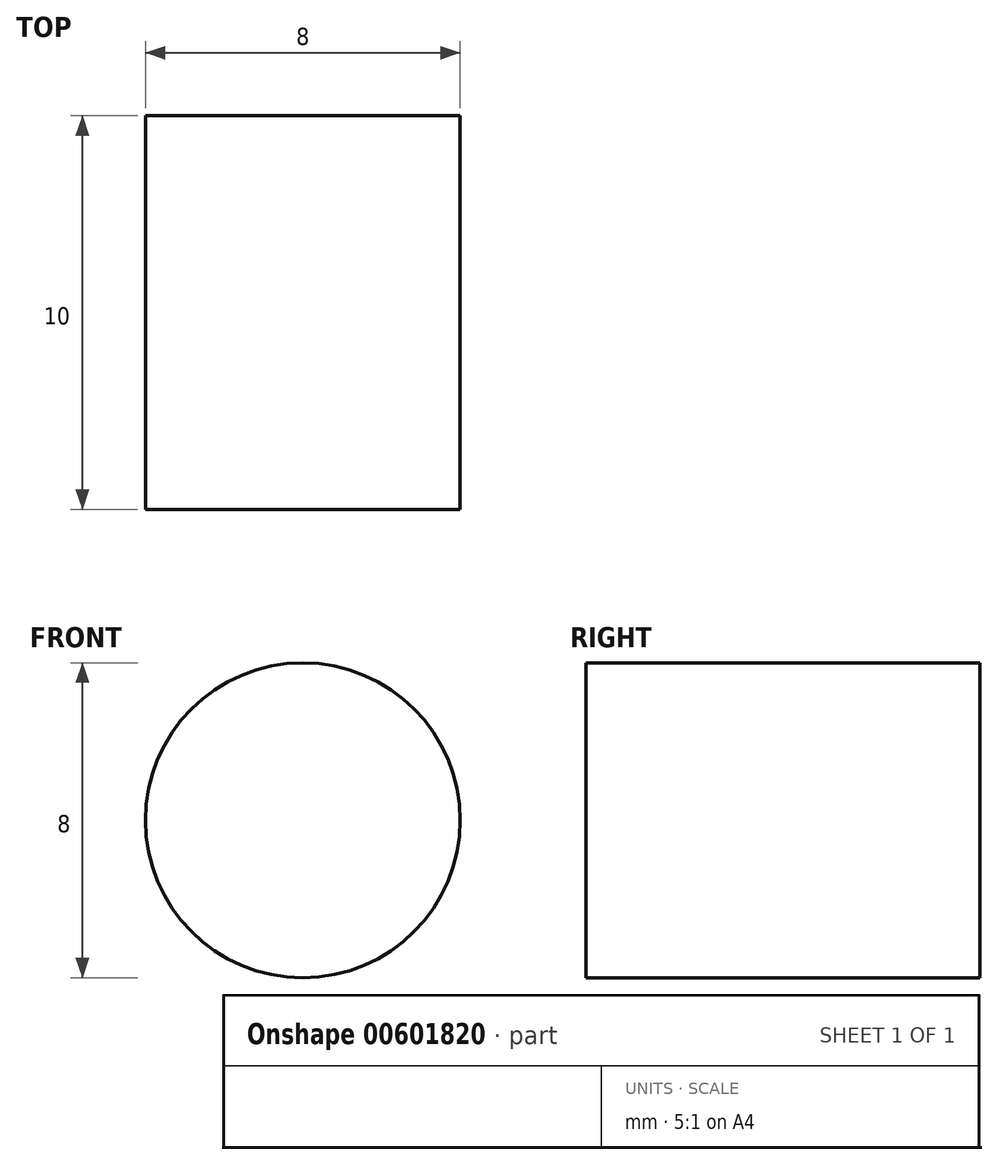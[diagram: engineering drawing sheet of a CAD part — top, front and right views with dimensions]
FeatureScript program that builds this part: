
annotation { "Feature Type Name" : "Feature", "Feature Type Description" : "" }
export const myFeature = defineFeature(function(context is Context, id is Id, definition is map)
    precondition{}
    {
        {
            var Q0;
            Q0=qCreatedBy(makeId("Front.planeOp"),FACE);
            var sketch = newSketch(context, id + "F0", { "sketchPlane" : qUnion([Q0])});
            skCircle(sketch, "E0", {"center": v(0, 0) * mm, "radius": 4 * mm});
            skSolve(sketch);
        }
        {
            var Q0;
            Q0=makeQuery(id+"F0.imprint","IMPRINT",FACE,{"disambiguationData":[TD([[makeQuery(id+"F0.imprint","IMPRINT",EDGE,{"derivedFrom":sQuery(id+"F0.wireOp",EDGE,"E0")}),1.0]])]});
            extrude(context, id + "F1", {"entities" : qUnion([Q0]), "depth" : 10 * mm, "offsetDistance" : 25 * mm});
        }
    });
